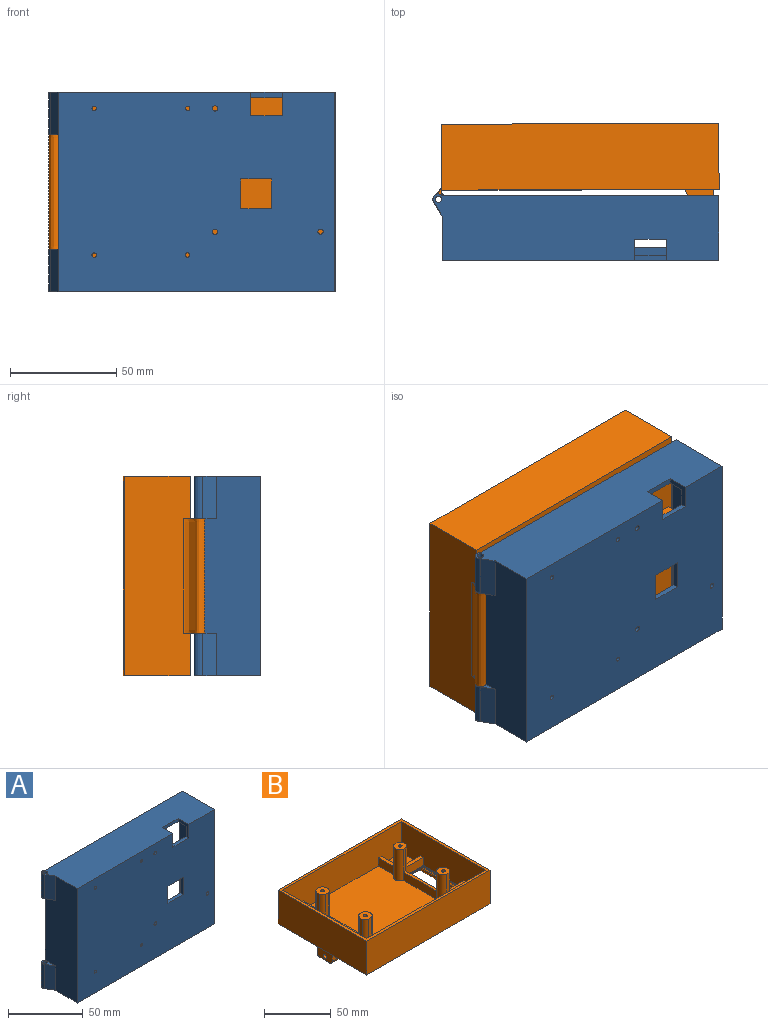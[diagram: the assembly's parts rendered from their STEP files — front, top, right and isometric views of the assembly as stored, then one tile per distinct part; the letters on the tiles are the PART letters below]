
ASSEMBLY  parts=2 mates=1
PART A: 144 faces, bbox 134.4x31.3x93.9 mm
  f0: plane 88.8x28mm, normal (-1,0,0), area 1712.4mm2, adj f3,f5,f7,f15,f76,f77,f78,f79
  f1: plane 93.89x30.5mm, normal (-1,0,0), area 2478.3mm2, adj f7,f8,f10,f11,f105,f106,f109,f112
  f2: plane 88.89x28mm, normal (-1,0,0), area 2091.2mm2, adj f6,f7,f9,f13,f15,f29,f32,f33
  f3: plane 6.09x2.5mm, normal (0,1,0), area 15.2mm2, adj f0,f4,f76,f77
  f4: plane 88.8x28mm, normal (1,0,0), area 1727.5mm2, adj f3,f7,f9,f15,f76,f77,f78,f79
  f5: plane 62.5x28mm, normal (0,0,1), area 1750mm2, adj f0,f7,f14,f15
  f6: plane 8.03x1.72mm, normal (0,0,-1), area 4.9mm2, adj f2,f7,f31,f33,f34,f35,f36,f37
  f7: plane 130.16x93.89mm, normal (0,1,0), area 1145.7mm2, adj f0,f1,f2,f4,f5,f6,f8,f9
  f8: plane 134.43x31.27mm, normal (0,0,-1), area 3054.3mm2, adj f1,f7,f10,f12,f24,f25,f26,f27
  f9: plane 60.16x28mm, normal (0,0,1), area 749mm2, adj f2,f4,f7,f15,f24,f25,f26,f27
  f10: plane 130.16x93.89mm, normal (0,-1,0), area 11823.5mm2, adj f1,f8,f11,f12,f16,f17,f18,f19
  f11: plane 134.43x31.27mm, normal (0,0,1), area 3840.3mm2, adj f1,f7,f10,f12,f20,f22,f23,f110
  f12: plane 93.89x30.5mm, normal (1,0,0), area 2410.5mm2, adj f7,f8,f10,f11,f41,f129,f130,f131
  f13: plane 125.16x28mm, normal (0,0,-1), area 3392.3mm2, adj f2,f7,f14,f15,f20,f22,f23
  f14: plane 88.89x28mm, normal (1,0,0), area 2489mm2, adj f5,f7,f13,f15
  f15: plane 125.16x88.89mm, normal (0,1,0), area 10089.6mm2, adj f0,f2,f4,f5,f9,f13,f14,f16
  f16: plane 14.5x2.5mm, normal (0,0,-1), area 36.2mm2, adj f10,f15,f17,f19
  f17: plane 14x2.5mm, normal (-1,0,0), area 35mm2, adj f10,f15,f16,f18
  f18: plane 14.5x2.5mm, normal (0,0,1), area 36.2mm2, adj f10,f15,f17,f19
  f19: plane 14x2.5mm, normal (1,0,0), area 35mm2, adj f10,f15,f16,f18
  f20: plane 11.09x10mm, normal (-1,0,0), area 46.5mm2, adj f10,f11,f13,f15,f21,f23
  f21: plane 14.95x2.5mm, normal (0,0,1), area 37.4mm2, adj f10,f15,f20,f22
  f22: plane 11.09x10mm, normal (1,0,0), area 46.5mm2, adj f10,f11,f13,f15,f21,f23
  f23: plane 14.95x2.5mm, normal (0,-1,0), area 37.4mm2, adj f11,f13,f20,f22
  f24: plane 17.6x2.5mm, normal (1,0,0), area 44mm2, adj f8,f9,f25,f27
  f25: plane 53.15x2.5mm, normal (0,-1,0), area 132.9mm2, adj f8,f9,f24,f26
  f26: plane 17.6x2.5mm, normal (-1,0,0), area 44mm2, adj f8,f9,f25,f27
  f27: plane 53.15x2.5mm, normal (0,1,0), area 132.9mm2, adj f8,f9,f24,f26
  f28: cylinder r=3.72mm len=7.45mm, axis (1,0,0), area 1.9mm2, adj f30,f143
  f29: cylinder r=4.55mm len=9.1mm, axis (1,0,0), area 11.7mm2, adj f2,f30
  f30: cone r=3.72mm half-angle=45deg, axis (-1,0,0), area 30.4mm2, adj f28,f29
  f31: plane 10.99x0.8mm, normal (-1,0,0), area 8.8mm2, adj f6,f7,f32,f34
  f32: plane 8.03x1.72mm, normal (0,0,1), area 4.9mm2, adj f2,f7,f31,f33,f34,f35,f36,f37
  f33: plane 10.99x0.66mm, normal (-0.92,0.38,0), area 7.8mm2, adj f2,f6,f32,f35
  f34: plane 10.99x0.8mm, normal (0,1,0), area 8.8mm2, adj f6,f31,f32,f40
  f35: plane 10.99x0.05mm, normal (-0.71,0.71,0), area 0.7mm2, adj f6,f32,f33,f36
  f36: plane 10.99x0.05mm, normal (0,1,0), area 0.5mm2, adj f6,f32,f35,f37
  f37: plane 10.99x4.33mm, normal (-1,0,0), area 37.4mm2, adj f6,f32,f36,f38,f41
  f38: plane 10.99x0.5mm, normal (-0.71,0.71,0), area 7.8mm2, adj f6,f32,f37,f39
  f39: plane 10.99x0.05mm, normal (0,1,0), area 0.5mm2, adj f6,f32,f38,f40
  f40: plane 10.99x1.7mm, normal (-1,0,0), area 18.7mm2, adj f6,f32,f34,f39
  f41: cylinder r=1.8mm len=3.6mm, axis (-1,0,0), area 24.1mm2, adj f12,f37
  f42: plane 4.66x0.08mm, normal (0,0,-1), area 0.4mm2, adj f43,f49,f57,f142
  f43: plane 2.56x2.56mm, normal (0,0.71,-0.71), area 0.3mm2, adj f42,f44,f55,f140
  f44: plane 11.09x0.08mm, normal (0,1,0), area 0.9mm2, adj f43,f48,f54,f138
  f45: plane 5.91x0.47mm, normal (0,0,1), area 2.7mm2, adj f2,f46,f52,f55,f57
  f46: plane 17.99x0.46mm, normal (0,1,0), area 8.3mm2, adj f2,f45,f47,f59
  f47: plane 5.91x0.46mm, normal (0,0,-1), area 2.7mm2, adj f2,f46,f51,f58
  f48: plane 2.57x2.54mm, normal (0,0.71,0.7), area 0.3mm2, adj f44,f50,f56,f137
  f49: plane 16.22x0.08mm, normal (0,-1,0), area 1.3mm2, adj f42,f50,f59,f141
  f50: plane 4.67x0.08mm, normal (0,0,1), area 0.4mm2, adj f48,f49,f58,f139
  f51: plane 3.02x3.02mm, normal (0,-0.71,-0.71), area 2mm2, adj f2,f47,f53,f56,f58
  f52: plane 3.02x3.02mm, normal (0,-0.71,0.71), area 2mm2, adj f2,f45,f53,f55
  f53: plane 11.95x0.49mm, normal (0,-1,0), area 5.1mm2, adj f2,f51,f52,f54,f55,f56
  f54: plane 11.79x0.84mm, normal (-0.71,0.71,0), area 13.6mm2, adj f44,f53,f55,f56
  f55: plane 3.44x3.4mm, normal (-0.71,0.5,-0.5), area 5mm2, adj f43,f45,f52,f53,f54,f57
  f56: plane 3.45x3.38mm, normal (-0.71,0.5,0.5), area 5mm2, adj f48,f51,f53,f54,f58
  f57: plane 5.91x0.88mm, normal (-0.71,0,-0.71), area 6.6mm2, adj f42,f45,f55,f59
  f58: plane 5.92x0.88mm, normal (-0.71,0,0.71), area 6.6mm2, adj f47,f50,f51,f56,f59
  f59: plane 17.99x0.88mm, normal (-0.71,-0.71,0), area 21.3mm2, adj f46,f49,f57,f58
  f60: plane 4.6x4.6mm, normal (0,1,0), area 11.7mm2, adj f61,f74
  f61: cylinder r=1.25mm len=6mm, axis (0,-1,0), area 47.1mm2, adj f10,f60
  f62: cylinder r=4.3mm len=8.6mm, axis (0,-1,0), area 40.5mm2, adj f15,f74
  f63: plane 4.6x4.6mm, normal (0,1,0), area 13.2mm2, adj f64,f75
  f64: cylinder r=1.04mm len=3.5mm, axis (0,-1,0), area 22.8mm2, adj f63,f66
  f65: cylinder r=4.3mm len=8.6mm, axis (0,-1,0), area 36.9mm2, adj f2,f15,f75
  f66: plane 2.08x2.08mm, normal (0,1,0), area 3.4mm2, adj f64
  f67: plane 4.6x4.6mm, normal (0,1,0), area 11.7mm2, adj f73,f104
  f68: cylinder r=4.3mm len=8.6mm, axis (0,-1,0), area 36.9mm2, adj f2,f15,f73
  f69: plane 4.6x4.6mm, normal (0,1,0), area 11.7mm2, adj f70,f72
  f70: cylinder r=1.25mm len=6mm, axis (0,-1,0), area 47.1mm2, adj f10,f69
  f71: cylinder r=4.3mm len=8.6mm, axis (0,-1,0), area 40.5mm2, adj f15,f72
  f72: cone r=2.3mm half-angle=45deg, axis (0,-1,0), area 58.6mm2, adj f69,f71
  f73: cone r=2.3mm half-angle=45deg, axis (0,-1,0), area 58.3mm2, adj f2,f67,f68
  f74: cone r=2.3mm half-angle=45deg, axis (0,-1,0), area 58.6mm2, adj f60,f62
  f75: cone r=2.3mm half-angle=45deg, axis (0,-1,0), area 58.3mm2, adj f2,f63,f65
  f76: plane 28x2.5mm, normal (0,0,1), area 70mm2, adj f0,f3,f4,f15
  f77: plane 13.81x2.5mm, normal (0,0,-1), area 34.5mm2, adj f0,f3,f4,f79
  f78: plane 13.81x2.5mm, normal (0,0,1), area 34.5mm2, adj f0,f4,f7,f79
  f79: plane 54.96x2.5mm, normal (0,1,0), area 137.4mm2, adj f0,f4,f77,f78
  f80: plane 1.3x0.08mm, normal (0,0,1), area 0.1mm2, adj f81,f95,f96,f135
  f81: cylinder r=2.33mm len=2.33mm, axis (1,0,0), area 0.3mm2, adj f80,f82,f97,f136
  f82: plane 5.8x0.08mm, normal (0,-1,0), area 0.5mm2, adj f81,f83,f99,f134
  f83: cylinder r=2.33mm len=2.33mm, axis (1,0,0), area 0.3mm2, adj f82,f84,f101,f132
  f84: plane 1.3x0.08mm, normal (0,0,-1), area 0.1mm2, adj f83,f85,f103,f130
  f85: cylinder r=2.33mm len=2.33mm, axis (1,0,0), area 0.3mm2, adj f84,f86,f102,f129
  f86: plane 5.8x0.08mm, normal (0,1,0), area 0.5mm2, adj f85,f95,f100,f131
  f87: plane 1.3x0.45mm, normal (0,0,-1), area 0.6mm2, adj f2,f88,f94,f96
  f88: cylinder r=3.2mm len=3.2mm, axis (1,0,0), area 2.2mm2, adj f2,f87,f89,f98
  f89: plane 5.8x0.45mm, normal (0,-1,0), area 2.6mm2, adj f2,f88,f90,f100
  f90: cylinder r=3.2mm len=3.2mm, axis (1,0,0), area 2.2mm2, adj f2,f89,f91,f102
  f91: plane 1.3x0.45mm, normal (0,0,1), area 0.6mm2, adj f2,f90,f92,f103
  f92: cylinder r=3.2mm len=3.2mm, axis (1,0,0), area 2.4mm2, adj f2,f91,f93,f99,f101,f103
  f93: plane 5.8x0.51mm, normal (0,1,0), area 2.9mm2, adj f2,f92,f94,f99
  f94: cylinder r=3.2mm len=3.2mm, axis (1,0,0), area 2.4mm2, adj f2,f87,f93,f96,f97,f99
  f95: cylinder r=2.33mm len=2.33mm, axis (1,0,0), area 0.3mm2, adj f80,f86,f98,f133
  f96: plane 1.31x0.87mm, normal (-0.71,0,0.71), area 1.6mm2, adj f80,f87,f94,f97,f98
  f97: cone r=2.33mm half-angle=45deg, axis (-1,0,0), area 5.5mm2, adj f81,f94,f96,f99
  f98: cone r=3.33mm half-angle=45deg, axis (-1,0,0), area 5.3mm2, adj f88,f95,f96,f100
  f99: plane 5.8x0.92mm, normal (-0.71,-0.71,0), area 7.6mm2, adj f82,f92,f93,f94,f97,f101
  f100: plane 5.8x0.87mm, normal (-0.71,0.71,0), area 7.1mm2, adj f86,f89,f98,f102
  f101: cone r=3.33mm half-angle=45deg, axis (-1,0,0), area 5.5mm2, adj f83,f92,f99,f103
  f102: cone r=2.33mm half-angle=45deg, axis (-1,0,0), area 5.3mm2, adj f85,f90,f100,f103
  f103: plane 1.31x0.87mm, normal (-0.71,0,-0.71), area 1.6mm2, adj f84,f91,f92,f101,f102
  f104: cylinder r=1.25mm len=6mm, axis (0,1,0), area 47.1mm2, adj f10,f67
  f105: plane 10.42x4.27mm, normal (0,0,1), area 20mm2, adj f1,f106,f107,f108
  f106: plane 20x6.25mm, normal (-0.86,-0.5,0), area 144.6mm2, adj f1,f8,f105,f108
  f107: cylinder r=1.5mm len=20mm, axis (0,0,-1), area 188.5mm2, adj f8,f105
  f108: extruded ~20x4.27mm, area 154.4mm2, adj f7,f8,f105,f106
  f109: plane 10.42x4.27mm, normal (0,0,-1), area 20mm2, adj f1,f110,f111,f112
  f110: extruded ~19.94x4.27mm, area 153.9mm2, adj f7,f11,f109,f112
  f111: cylinder r=1.5mm len=19.94mm, axis (0,0,1), area 187.9mm2, adj f11,f109
  f112: plane 19.94x6.25mm, normal (-0.86,-0.5,0), area 144.2mm2, adj f1,f11,f109,f110
  f113: plane 5x5mm, normal (0,1,0), area 16.3mm2, adj f114,f128
  f114: cylinder r=1.04mm len=6mm, axis (0,-1,0), area 39.1mm2, adj f10,f113
  f115: cylinder r=4.5mm len=9mm, axis (0,-1,0), area 36mm2, adj f0,f15,f128
  f116: plane 4.93x4.93mm, normal (0,1,0), area 15.6mm2, adj f117,f127
  f117: cylinder r=1.05mm len=6mm, axis (0,-1,0), area 39.7mm2, adj f10,f116
  f118: cylinder r=4.46mm len=8.93mm, axis (0,-1,0), area 42.1mm2, adj f15,f127
  f119: plane 5x5mm, normal (0,1,0), area 16.3mm2, adj f120,f125
  f120: cylinder r=1.04mm len=6mm, axis (0,-1,0), area 39.1mm2, adj f10,f119
  f121: cylinder r=4.5mm len=9mm, axis (0,-1,0), area 36mm2, adj f0,f15,f125
  f122: plane 5x5mm, normal (0,1,0), area 16.3mm2, adj f123,f126
  f123: cylinder r=1.04mm len=6mm, axis (0,-1,0), area 39.1mm2, adj f10,f122
  f124: cylinder r=4.5mm len=9mm, axis (0,-1,0), area 42.4mm2, adj f15,f126
  f125: cone r=2.5mm half-angle=45deg, axis (0,-1,0), area 60.2mm2, adj f0,f119,f121
  f126: cone r=2.5mm half-angle=45deg, axis (0,-1,0), area 62.2mm2, adj f122,f124
  f127: cone r=2.46mm half-angle=45deg, axis (0,-1,0), area 61.5mm2, adj f116,f118
  f128: cone r=2.5mm half-angle=45deg, axis (0,-1,0), area 60.2mm2, adj f0,f113,f115
  f129: torus R=4.33mm, axis (-1,0,0), area 15.1mm2, adj f12,f85,f130,f131
  f130: cylinder r=2mm len=2mm, axis (0,-1,0), area 4.1mm2, adj f12,f84,f129,f132
  f131: cylinder r=2mm len=5.8mm, axis (0,0,-1), area 18.2mm2, adj f12,f86,f129,f133
  f132: torus R=4.33mm, axis (-1,0,0), area 14.9mm2, adj f12,f83,f130,f134
  f133: torus R=4.33mm, axis (-1,0,0), area 15.1mm2, adj f12,f95,f131,f135
  f134: cylinder r=2mm len=5.8mm, axis (0,0,-1), area 18.2mm2, adj f12,f82,f132,f136
  f135: cylinder r=2mm len=2mm, axis (0,1,0), area 4.1mm2, adj f12,f80,f133,f136
  f136: torus R=4.33mm, axis (-1,0,0), area 14.9mm2, adj f12,f81,f134,f135
  f137: cylinder r=2mm len=5.16mm, axis (0,0.7,-0.71), area 13.3mm2, adj f12,f48,f138,f139
  f138: cylinder r=2mm len=12.74mm, axis (0,0,-1), area 36.7mm2, adj f12,f44,f137,f140
  f139: cylinder r=2mm len=7.51mm, axis (0,1,0), area 17.9mm2, adj f12,f50,f137,f141
  f140: cylinder r=2mm len=5.14mm, axis (0,-0.71,-0.71), area 13.3mm2, adj f12,f43,f138,f142
  f141: cylinder r=2mm len=20.22mm, axis (0,0,1), area 55.5mm2, adj f12,f49,f139,f142
  f142: cylinder r=2mm len=7.49mm, axis (0,-1,0), area 17.9mm2, adj f12,f42,f140,f141
  f143: torus R=5.72mm, axis (-1,0,0), area 87.8mm2, adj f12,f28
PART B: 107 faces, bbox 135x94.2x42.3 mm
  f0: plane 88.89x79.33mm, normal (0,0,1), area 6932.8mm2, adj f4,f6,f37,f46,f52,f55,f58,f65
  f1: plane 65.64x21.75mm, normal (0,0,1), area 706mm2, adj f4,f5,f14,f15,f16,f17,f59,f61
  f2: plane 21.38x20.25mm, normal (0,0,1), area 425.9mm2, adj f5,f6,f56,f62,f95
  f3: plane 88.89x18.76mm, normal (0,0,1), area 1524.4mm2, adj f4,f6,f13,f38,f40,f41,f42,f44
  f4: plane 125.36x28.5mm, normal (0,1,0), area 3525.5mm2, adj f0,f1,f3,f5,f9,f13,f51,f52
  f5: plane 88.89x28.5mm, normal (-1,0,0), area 2510.9mm2, adj f1,f2,f4,f6,f9,f60,f61,f62
  f6: plane 125.36x28.5mm, normal (0,-1,0), area 3525.5mm2, adj f0,f2,f3,f5,f9,f13,f36,f37
  f7: plane 130.36x93.89mm, normal (0,0,-1), area 11155.9mm2, adj f8,f10,f11,f12,f18,f19,f20,f21
  f8: plane 93.89x31mm, normal (1,0,0), area 2737.7mm2, adj f7,f9,f10,f12,f23,f24,f26
  f9: plane 130.36x93.89mm, normal (0,0,1), area 1096.3mm2, adj f4,f5,f6,f8,f10,f11,f12,f13
  f10: plane 130.36x31mm, normal (0,-1,0), area 4041.3mm2, adj f7,f8,f9,f11
  f11: plane 93.89x31mm, normal (-1,0,0), area 2910.7mm2, adj f7,f9,f10,f12
  f12: plane 130.36x31mm, normal (0,1,0), area 4041.3mm2, adj f7,f8,f9,f11
  f13: plane 88.89x28.5mm, normal (1,0,0), area 2533.4mm2, adj f3,f4,f6,f9
  f14: plane 15.29x0.5mm, normal (0,1,0), area 7.6mm2, adj f1,f15,f17,f18
  f15: plane 41.01x0.5mm, normal (1,0,0), area 20.5mm2, adj f1,f14,f16,f19
  f16: plane 15.29x0.5mm, normal (0,-1,0), area 7.6mm2, adj f1,f15,f17,f21
  f17: plane 41.01x0.5mm, normal (-1,0,0), area 20.5mm2, adj f1,f14,f16,f20
  f18: cylinder r=2mm len=19.29mm, axis (-1,0,0), area 52.6mm2, adj f7,f14,f19,f20
  f19: cylinder r=2mm len=45.01mm, axis (0,1,0), area 133.4mm2, adj f7,f15,f18,f21
  f20: cylinder r=2mm len=45.01mm, axis (0,-1,0), area 133.4mm2, adj f7,f17,f18,f21
  f21: cylinder r=2mm len=19.29mm, axis (1,0,0), area 52.6mm2, adj f7,f16,f19,f20
  f22: plane 53.89x1.54mm, normal (-1,0,0), area 83mm2, adj f7,f23,f24,f25
  f23: plane 9.99x5.24mm, normal (0,-1,0), area 17.6mm2, adj f8,f22,f25,f26,f27,f28
  f24: plane 9.99x5.24mm, normal (0,1,0), area 17.6mm2, adj f8,f22,f25,f26,f27,f28
  f25: extruded ~53.89x0.96mm, area 73.6mm2, adj f22,f23,f24,f27
  f26: extruded ~53.89x9.98mm, area 969.5mm2, adj f8,f23,f24,f27
  f27: plane 53.89x0.96mm, normal (0,0,-1), area 51.7mm2, adj f23,f24,f25,f26
  f28: cylinder r=1.5mm len=53.89mm, axis (0,1,0), area 507.9mm2, adj f23,f24
  f29: plane 10x8.37mm, normal (0,0,-1), area 83.7mm2, adj f31,f32,f34,f35
  f30: plane 13.5x8mm, normal (0,1,0), area 93.1mm2, adj f7,f31,f32,f34
  f31: plane 16.32x11.32mm, normal (0.91,0,-0.42), area 180.9mm2, adj f7,f29,f30,f33,f34,f35,f106
  f32: plane 16x11mm, normal (-1,0,0), area 163.9mm2, adj f7,f29,f30,f33,f34,f35,f106
  f33: plane 13.5x8mm, normal (0,-1,0), area 93.1mm2, adj f7,f31,f32,f35
  f34: cylinder r=3mm len=9.77mm, axis (-1,0,0), area 41.8mm2, adj f29,f30,f31,f32
  f35: cylinder r=3mm len=9.77mm, axis (1,0,0), area 41.8mm2, adj f29,f31,f32,f33
  f36: plane 17.04x3.31mm, normal (0,0,1), area 56.3mm2, adj f6,f37,f38,f70
  f37: plane 17.04x7.5mm, normal (1,0,0), area 127.8mm2, adj f0,f6,f36,f75
  f38: plane 17.03x7.5mm, normal (-1,0,0), area 127.7mm2, adj f3,f6,f36,f76
  f39: plane 15.42x3.05mm, normal (0,0,1), area 47mm2, adj f40,f41,f42,f71
  f40: plane 15.41x7.5mm, normal (0,1,0), area 115.6mm2, adj f3,f39,f41,f76
  f41: plane 7.5x3.05mm, normal (-1,0,0), area 22.8mm2, adj f3,f39,f40,f42
  f42: plane 15.42x7.5mm, normal (0,-1,0), area 115.7mm2, adj f3,f39,f41,f74
  f43: plane 36x3.29mm, normal (0,0,1), area 116.2mm2, adj f44,f45,f46,f72,f79
  f44: plane 18x7.5mm, normal (-1,0,0), area 135mm2, adj f3,f43,f45,f74
  f45: plane 18x7.5mm, normal (-1,0,0), area 135mm2, adj f3,f43,f44,f84
  f46: plane 36x7.5mm, normal (1,0,0), area 270mm2, adj f0,f43,f75,f83
  f47: plane 15.43x3.09mm, normal (0,0,1), area 47mm2, adj f48,f49,f50,f80
  f48: plane 7.5x3.05mm, normal (-1,0,0), area 22.8mm2, adj f3,f47,f49,f50
  f49: plane 15.41x7.5mm, normal (0,-1,0), area 115.6mm2, adj f3,f47,f48,f85
  f50: plane 15.42x7.5mm, normal (0,1,0), area 115.7mm2, adj f3,f47,f48,f84
  f51: plane 16.96x3.36mm, normal (0,0,1), area 56.1mm2, adj f4,f52,f53,f81
  f52: plane 16.96x7.5mm, normal (1,0,0), area 127.2mm2, adj f0,f4,f51,f83
  f53: plane 16.96x7.5mm, normal (-1,0,0), area 127.2mm2, adj f3,f4,f51,f85
  f54: plane 16.99x3mm, normal (0,0,1), area 50.9mm2, adj f6,f55,f56,f88
  f55: plane 16.98x7.5mm, normal (-1,0,0), area 127.3mm2, adj f0,f6,f54,f92
  f56: plane 16.99x7.5mm, normal (1,0,0), area 127.4mm2, adj f2,f6,f54,f95
  f57: plane 36x2.47mm, normal (0,0,1), area 87mm2, adj f58,f59,f89,f97
  f58: plane 36x7.5mm, normal (-1,0,0), area 270mm2, adj f0,f57,f92,f101
  f59: plane 36x7.5mm, normal (1,0,0), area 270mm2, adj f1,f57,f93,f103
  f60: plane 18.13x3mm, normal (0,0,1), area 54.4mm2, adj f5,f61,f62,f90
  f61: plane 18.13x7.5mm, normal (0,-1,0), area 136mm2, adj f1,f5,f60,f93
  f62: plane 18.13x7.5mm, normal (0,1,0), area 136mm2, adj f2,f5,f60,f95
  f63: plane 16.67x3.05mm, normal (0,0,1), area 50mm2, adj f4,f64,f65,f98
  f64: plane 16.67x7.5mm, normal (1,0,0), area 125mm2, adj f1,f4,f63,f102
  f65: plane 16.67x7.5mm, normal (-1,0,0), area 125mm2, adj f0,f4,f63,f101
  f66: plane 18.14x3.05mm, normal (0,0,1), area 54.4mm2, adj f67,f68,f69,f99
  f67: plane 18.13x7.5mm, normal (0,-1,0), area 136mm2, adj f1,f66,f68,f102
  f68: plane 7.5x3mm, normal (1,0,0), area 22.5mm2, adj f1,f66,f67,f69
  f69: plane 18.13x7.5mm, normal (0,1,0), area 136mm2, adj f1,f66,f68,f103
  f70: plane 21x3.31mm, normal (0,1,0), area 69.5mm2, adj f36,f73,f75,f76
  f71: plane 21x3.05mm, normal (-1,0,0), area 64mm2, adj f39,f73,f74,f76
  f72: plane 21x3.24mm, normal (0,-1,0), area 68.1mm2, adj f43,f73,f74,f75
  f73: plane 9.77x9.46mm, normal (0,0,1), area 70.8mm2, adj f70,f71,f72,f74,f75,f76,f77
  f74: cylinder r=5mm len=28.5mm, axis (0,0,-1), area 131.8mm2, adj f3,f42,f44,f71,f72,f73
  f75: cylinder r=5mm len=28.5mm, axis (0,0,-1), area 352.5mm2, adj f0,f37,f46,f70,f72,f73
  f76: cylinder r=5mm len=28.5mm, axis (0,0,-1), area 132.7mm2, adj f3,f38,f40,f70,f71,f73
  f77: cylinder r=1.38mm len=28.5mm, axis (0,0,-1), area 247.9mm2, adj f73,f78
  f78: plane 2.77x2.77mm, normal (0,0,1), area 6mm2, adj f77
  f79: plane 21x3.24mm, normal (0,1,0), area 68.1mm2, adj f43,f82,f83,f84
  f80: plane 21x3.05mm, normal (-1,0.01,0), area 64mm2, adj f47,f82,f84,f85
  f81: plane 21x3.31mm, normal (0,-1,0), area 69.5mm2, adj f51,f82,f83,f85
  f82: plane 9.77x9.45mm, normal (0,0,1), area 70.8mm2, adj f79,f80,f81,f83,f84,f85,f86
  f83: cylinder r=5mm len=28.5mm, axis (0,0,-1), area 352.5mm2, adj f0,f46,f52,f79,f81,f82
  f84: cylinder r=5mm len=28.5mm, axis (0,0,-1), area 131.8mm2, adj f3,f45,f50,f79,f80,f82
  f85: cylinder r=5mm len=28.5mm, axis (0,0,-1), area 132.7mm2, adj f3,f49,f53,f80,f81,f82
  f86: cylinder r=1.38mm len=28.5mm, axis (0,0,-1), area 247.9mm2, adj f82,f87
  f87: plane 2.77x2.77mm, normal (0,0,1), area 6mm2, adj f86
  f88: plane 21x3mm, normal (0,1,0), area 63mm2, adj f54,f91,f92,f95
  f89: plane 21x2.42mm, normal (0,-1,0), area 50.8mm2, adj f57,f91,f92,f93
  f90: plane 21x3mm, normal (1,0,0), area 63mm2, adj f60,f91,f93,f95
  f91: plane 9.77x9.63mm, normal (0,0,1), area 71.4mm2, adj f88,f89,f90,f92,f93,f94,f95
  f92: cylinder r=5mm len=28.5mm, axis (0,0,-1), area 369.8mm2, adj f0,f55,f58,f88,f89,f91
  f93: cylinder r=5mm len=28.5mm, axis (0,0,-1), area 145.8mm2, adj f1,f59,f61,f89,f90,f91
  f94: cylinder r=1.38mm len=28.5mm, axis (0,0,-1), area 247.9mm2, adj f91,f96
  f95: cylinder r=5mm len=28.5mm, axis (0,0,-1), area 136.5mm2, adj f2,f56,f62,f88,f90,f91
  f96: plane 2.77x2.77mm, normal (0,0,1), area 6mm2, adj f94
  f97: plane 21x2.42mm, normal (0,1,0), area 50.8mm2, adj f57,f100,f101,f103
  f98: plane 21x3mm, normal (0,-1,0), area 63mm2, adj f63,f100,f101,f102
  f99: plane 21x3mm, normal (1,0,0), area 63mm2, adj f66,f100,f102,f103
  f100: plane 9.77x9.62mm, normal (0,0,1), area 71.4mm2, adj f97,f98,f99,f101,f102,f103,f104
  f101: cylinder r=5mm len=28.5mm, axis (0,0,-1), area 369.8mm2, adj f0,f58,f65,f97,f98,f100
  f102: cylinder r=5mm len=28.5mm, axis (0,0,-1), area 136.5mm2, adj f1,f64,f67,f98,f99,f100
  f103: cylinder r=5mm len=28.5mm, axis (0,0,-1), area 145.8mm2, adj f1,f59,f69,f97,f99,f100
  f104: cylinder r=1.38mm len=28.5mm, axis (0,0,-1), area 247.9mm2, adj f100,f105
  f105: plane 2.77x2.77mm, normal (0,0,1), area 6mm2, adj f104
  f106: cylinder r=1.62mm len=10.71mm, axis (-1,0,0), area 101.1mm2, adj f31,f32
PLACE A at identity fixed
PLACE B rot(axis=(0,-0.71,-0.71),179.9deg) t=(-69.78,33.21,0.75)mm
MATE revolute B.f28 <-> A.f107  axis (0,0,1) through (-121.93,28.77,20.53)mm
